MODEL slx_8d84f53810ac
CONFIG AbsTol = auto
CONFIG EnableMultiTasking = off
CONFIG FixedStep = 0.00001
CONFIG InitFcn = % 单位H，实际物理模型的电机"对应轴的电感"
Ls = 5.19338e-5;
% 单位Ω，实际物理模型的电机"相电阻"
Rs = 0.1906689107;

% 单位H，预测的电机“对应轴的电感”
Ls_pre = 5.29338e-5;
% 单位Ω，预测的电机“相电阻”
Rs_pre = 0.2306689107;

% 单位rad/s，一阶低通滤波的截止频率
wc = 2000;

% 单位s秒，控制周期的大小
T = 0.00005;
CONFIG MaxStep = auto
CONFIG MinStep = auto
CONFIG RelTol = 1e-3
CONFIG SampleTimeConstraint = Unconstrained
CONFIG SolverName = FixedStepAuto
CONFIG StartTime = 0.0
CONFIG StopTime = 0.1
BLOCK [CCaller] C Caller4
  FunctionName = SguanIMC_Loop
  PortSpecificationStruct = %)30     .    X ,   8    (     @         %    "     (    !     0         %  0 "0    $    _    07)G3F%M90  4&]R=$YA;64 4V-O<&4     26YD97@     5'EP90      4VEZ90      27-';&]B86P   X    X    !@    @    $          4    (     0    4    !         !     %    :6YP=70    .    .     8    (    !          %    "     $    %     0         0    !0   &EN<'5T    #@   #@    &    "     0         !0    @    !    !0...<+936ch>
BLOCK [DataTypeConversion] Data Type Conversion4
  OutDataTypeStr = single
  RndMeth = Floor
  SaturateOnIntegerOverflow = off
BLOCK [Delay] Delay4
  DelayLength = 1
  InputPortMap = u0
  NameLocation = left
BLOCK [Scope] Scope16
  ActiveDisplayYMaximum = 11.253331999942651
  ActiveDisplayYMinimum = -1.25037022221585
  DataLoggingVariableName = ScopeData17
  Floating = off
  GraphicalSettings = {"AxesScalingProperties":{"AlignXAxis":"Center","AlignYAxis":"Center","AutoScaleXAxisLimits":false,"AxesScaling":"Manual","AxesScalingNumUpdates":10,"ExpandOnly":true,"ScaleAxesLimitsAtStop":false,"XAxisDataRange":100,"YAxisDataRange":80},"DisplayProperties":{"ColorOrder":["auto","auto","auto","auto","auto","auto","auto","auto","auto","auto","auto","auto","auto","auto","auto","auto","auto","auto",...<+2014ch>
  MultipleDisplayCache = [{"MaxYLimMag":11.253331999942651,"MaxYLimReal":11.253331999942651,"MinYLimMag":0,"MinYLimReal":-1.25037022221585,"PlotAsMagnitudePhase":false,"ShowGrid":true,"ShowLegend":true,"Title":"%<SignalLabel>","YLabel":""}]
  NumInputPorts = 1
  ScopeFrameLocation = window
  ShowLegend = on
  Visible = on
  WasSavedAsWebScope = on
  WindowPosition = [1125.000000,174.000000,560.000000,420.000000,]
BLOCK [Step] Step
  After = 10
  SampleTime = 0
  Time = 0.03
BLOCK [Sum] Sum18
  Inputs = |+-
BLOCK [Sum] Sum19
  Inputs = -+|
  NameLocation = left
BLOCK [TransferFcn] Transfer Fcn1
  Denominator = [(1/Rs_pre) (wc/Rs_pre)]
  Numerator = [(wc*Ls_pre/Rs_pre) wc]
BLOCK [TransferFcn] Transfer Fcn25
  Denominator = [(Ls/Rs) 1]
  Numerator = [1/Rs]
BLOCK [ZeroOrderHold] Zero-Order Hold11
  SampleTime = T
LINE C Caller4:1 -> Sum19:1
LINE Data Type Conversion4:1 -> C Caller4:1
LINE Delay4:1 -> Sum18:2
LINE Step:1 -> Sum18:1
LINE Sum18:1 -> Transfer Fcn1:1
LINE Sum19:1 -> Delay4:1
LINE Transfer Fcn1:1 -> Zero-Order Hold11:1
LINE Transfer Fcn25:1 -> Scope16:1
LINE Transfer Fcn25:1 -> Sum19:2
LINE Zero-Order Hold11:1 -> Data Type Conversion4:1
LINE Zero-Order Hold11:1 -> Transfer Fcn25:1
